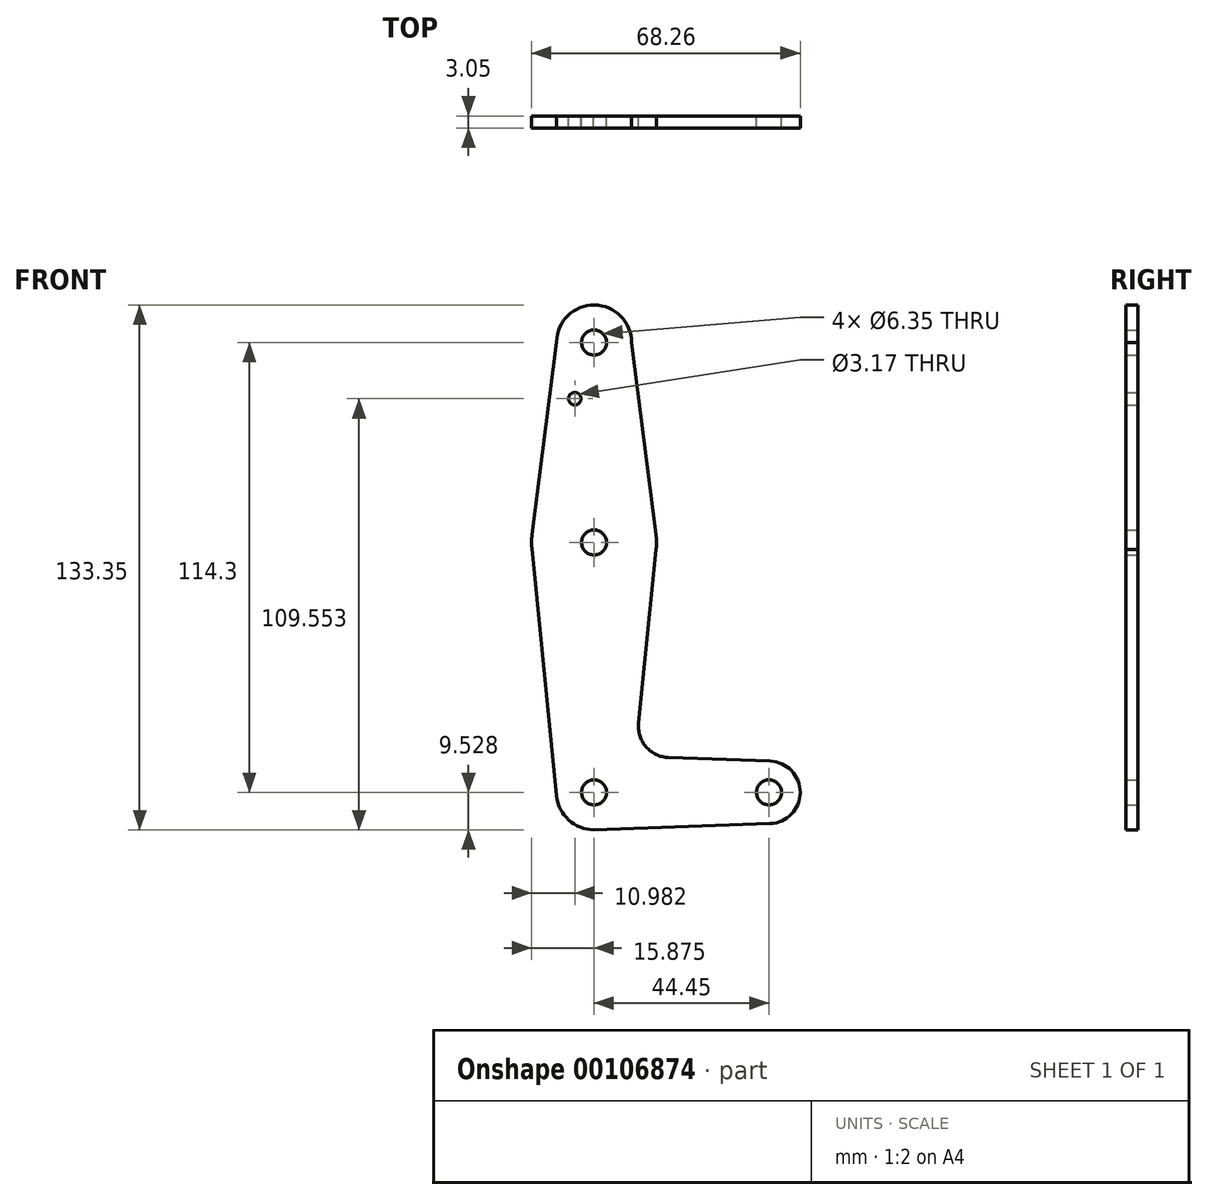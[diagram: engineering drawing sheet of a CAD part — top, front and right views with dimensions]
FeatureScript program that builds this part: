
annotation { "Feature Type Name" : "Feature", "Feature Type Description" : "" }
export const myFeature = defineFeature(function(context is Context, id is Id, definition is map)
    precondition{}
    {
        {
            var Q0;
            Q0=qCreatedBy(makeId("Front.planeOp"),FACE);
            var sketch = newSketch(context, id + "F0", { "sketchPlane" : qUnion([Q0])});
            skLineSegment(sketch, "E0", {"start": v(-6.6, 67.29) * mm, "end": v(-6.6, -47.01) * mm, "construction": true});
            skLineSegment(sketch, "E1", {"start": v(-6.6, -47.01) * mm, "end": v(37.86, -47.01) * mm, "construction": true});
            skCircle(sketch, "E2", {"center": v(-6.6, 67.29) * mm, "radius": 9.53 * mm});
            skCircle(sketch, "E3", {"center": v(-6.6, 16.49) * mm, "radius": 15.88 * mm});
            skCircle(sketch, "E4", {"center": v(-6.6, -47.01) * mm, "radius": 9.53 * mm});
            skCircle(sketch, "E5", {"center": v(37.86, -47.01) * mm, "radius": 7.94 * mm});
            skLineSegment(sketch, "E6", {"start": v(-16.12, 67.45) * mm, "end": v(-22.34, 18.49) * mm});
            skLineSegment(sketch, "E7", {"start": v(2.93, 67.29) * mm, "end": v(9.15, 18.5) * mm});
            skLineSegment(sketch, "E8", {"start": v(9.18, 14.71) * mm, "end": v(4.71, -29.42) * mm});
            skLineSegment(sketch, "E9", {"start": v(-22.4, 14.98) * mm, "end": v(-16.07, -47.96) * mm});
            skLineSegment(sketch, "E10", {"start": v(12.34, -38.16) * mm, "end": v(38.14, -39.08) * mm});
            skLineSegment(sketch, "E11", {"start": v(-6.7, -56.54) * mm, "end": v(38.14, -54.94) * mm});
            skCircle(sketch, "E12", {"center": v(-6.6, 67.29) * mm, "radius": 3.18 * mm});
            skCircle(sketch, "E13", {"center": v(-11.49, 53.01) * mm, "radius": 1.59 * mm});
            skCircle(sketch, "E14", {"center": v(-6.6, 16.49) * mm, "radius": 3.18 * mm});
            skCircle(sketch, "E15", {"center": v(-6.6, -47.01) * mm, "radius": 3.18 * mm});
            skCircle(sketch, "E16", {"center": v(37.86, -47.01) * mm, "radius": 3.18 * mm});
            skArc(sketch, "E17.filletArc", {"start": v(4.71, -29.42) * mm, "mid": v(6.63, -35.44) * mm, "end": v(12.34, -38.16) * mm});
            skSolve(sketch);
        }
        {
            var Q0;
            {var subQ0=sQuery(id+"F0.wireOp",EDGE,"E9");var subQ1=sQuery(id+"F0.wireOp",EDGE,"E3");var subQ2=makeQuery(id+"F0.imprint","INTERSECT",VERTEX,{"disambiguationData":[OD(0.0)],"derivedFrom":[subQ1,subQ0]});Q0=makeQuery(id+"F0.imprint","IMPRINT",FACE,{"disambiguationData":[TD([[makeQuery(id+"F0.imprint","IMPRINT",EDGE,{"disambiguationData":[TD([[subQ2,-1.0]])],"derivedFrom":subQ1}),1.0]])]});}
            var Q1;
            {var subQ0=sQuery(id+"F0.wireOp",EDGE,"E11");var subQ1=sQuery(id+"F0.wireOp",EDGE,"E4");var subQ2=makeQuery(id+"F0.imprint","INTERSECT",VERTEX,{"disambiguationData":[OD(0.0)],"derivedFrom":[subQ1,subQ0]});Q1=makeQuery(id+"F0.imprint","IMPRINT",FACE,{"disambiguationData":[TD([[makeQuery(id+"F0.imprint","IMPRINT",EDGE,{"disambiguationData":[TD([[subQ2,-1.0]])],"derivedFrom":subQ1}),1.0]])]});}
            var Q2;
            Q2=makeQuery(id+"F0.imprint","IMPRINT",FACE,{"disambiguationData":[TD([[makeQuery(id+"F0.imprint","IMPRINT",EDGE,{"derivedFrom":sQuery(id+"F0.wireOp",EDGE,"E12")}),-1.0]])]});
            var Q3;
            Q3=makeQuery(id+"F0.imprint","IMPRINT",FACE,{"disambiguationData":[TD([[makeQuery(id+"F0.imprint","IMPRINT",EDGE,{"derivedFrom":sQuery(id+"F0.wireOp",EDGE,"E14")}),-1.0]])]});
            var Q4;
            {var subQ0=sQuery(id+"F0.wireOp",EDGE,"E8");Q4=makeQuery(id+"F0.imprint","IMPRINT",FACE,{"disambiguationData":[TD([[makeQuery(id+"F0.imprint","IMPRINT",EDGE,{"derivedFrom":subQ0}),-1.0]])]});}
            var Q5;
            Q5=makeQuery(id+"F0.imprint","IMPRINT",FACE,{"disambiguationData":[TD([[makeQuery(id+"F0.imprint","IMPRINT",EDGE,{"derivedFrom":sQuery(id+"F0.wireOp",EDGE,"E15")}),-1.0]])]});
            var Q6;
            Q6=makeQuery(id+"F0.imprint","IMPRINT",FACE,{"disambiguationData":[TD([[makeQuery(id+"F0.imprint","IMPRINT",EDGE,{"derivedFrom":sQuery(id+"F0.wireOp",EDGE,"E16")}),-1.0]])]});
            var Q7;
            {var subQ1=sQuery(id+"F0.wireOp",EDGE,"E6");Q7=makeQuery(id+"F0.imprint","IMPRINT",FACE,{"disambiguationData":[TD([[makeQuery(id+"F0.imprint","IMPRINT",EDGE,{"derivedFrom":subQ1}),1.0]])]});}
            extrude(context, id + "F1", {"entities" : qUnion([Q0, Q1, Q2, Q3, Q4, Q5, Q6, Q7]), "depth" : 3.05 * mm});
        }
    });
